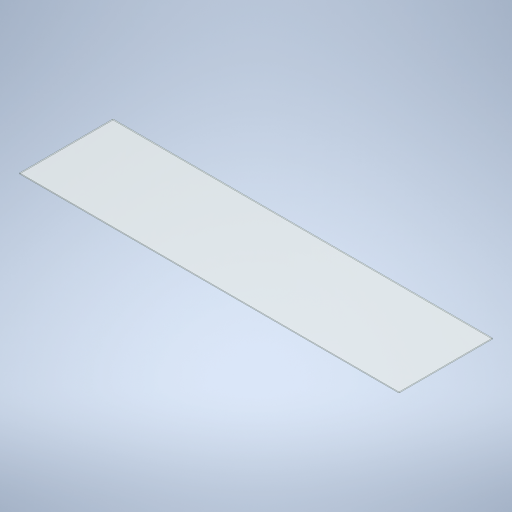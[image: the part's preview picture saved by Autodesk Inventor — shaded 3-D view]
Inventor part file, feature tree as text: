
AUTODESK INVENTOR PART (.ipt)
format: ipt  version: 2024 (Build 280153000, 153)  size: 233,472 bytes
history: native  units: in
note: dims shown in document units (in); Inventor stores cm internally (conversion verified against a paired STEP export)
features: extrude x1, sketch x1
ambient origin geometry x8: Origin, YZ Plane, XZ Plane, XY Plane, X Axis, Y Axis, Z Axis, Center Point
bodies: Solid1 (feature_tree)
feature tree (2):
  extrude  "Extrusion1"  Depth=291.5in
  sketch  "Sketch1"  dims[d2=71.787in d3=291.5in d4=0.75in d5=0.0in]
